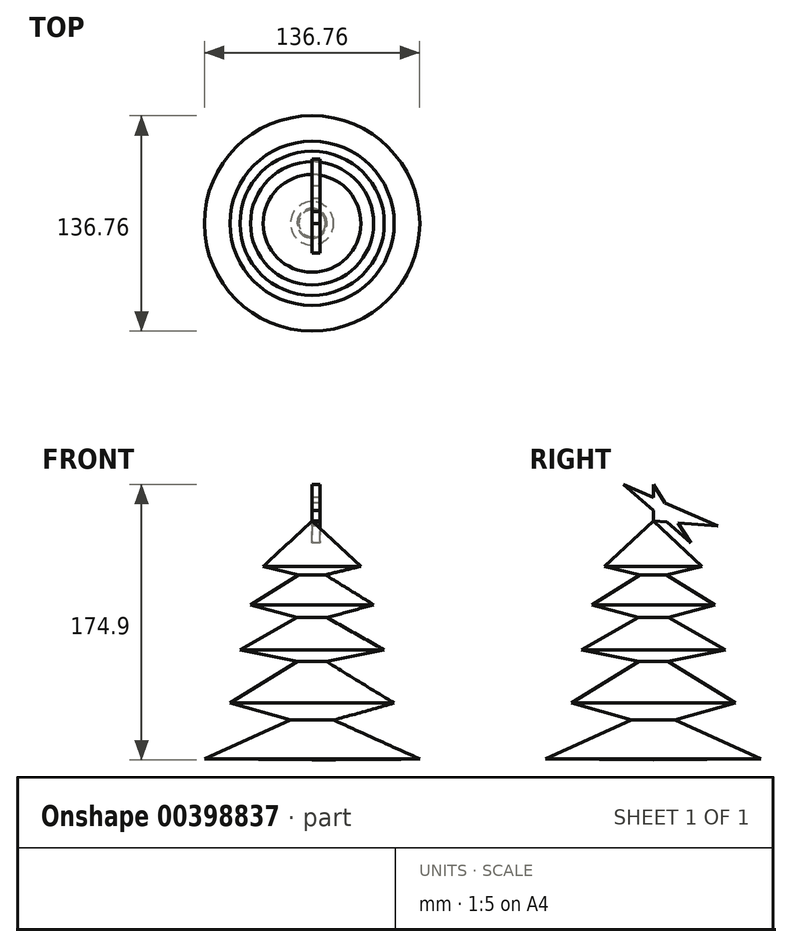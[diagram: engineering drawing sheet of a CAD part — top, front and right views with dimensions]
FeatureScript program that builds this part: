
annotation { "Feature Type Name" : "Feature", "Feature Type Description" : "" }
export const myFeature = defineFeature(function(context is Context, id is Id, definition is map)
    precondition{}
    {
        {
            var Q0;
            Q0=qCreatedBy(makeId("Front.planeOp"),FACE);
            var sketch = newSketch(context, id + "F0", { "sketchPlane" : qUnion([Q0])});
            skLineSegment(sketch, "E0", {"start": v(0, 75.99) * mm, "end": v(0, -75.59) * mm});
            skLineSegment(sketch, "E1", {"start": v(0, 75.99) * mm, "end": v(31.02, 47.38) * mm});
            skLineSegment(sketch, "E2", {"start": v(31.02, 47.38) * mm, "end": v(8.46, 41.92) * mm});
            skLineSegment(sketch, "E3", {"start": v(8.46, 41.92) * mm, "end": v(39.13, 22.93) * mm});
            skLineSegment(sketch, "E4", {"start": v(39.13, 22.93) * mm, "end": v(9.52, 14.73) * mm});
            skLineSegment(sketch, "E5", {"start": v(9.52, 14.73) * mm, "end": v(45.82, -5.8) * mm});
            skLineSegment(sketch, "E6", {"start": v(45.82, -5.8) * mm, "end": v(9.16, -13.22) * mm});
            skLineSegment(sketch, "E7", {"start": v(9.16, -13.22) * mm, "end": v(52.17, -39.58) * mm});
            skLineSegment(sketch, "E8", {"start": v(52.17, -39.58) * mm, "end": v(13.75, -50.32) * mm});
            skPoint(sketch, "E9.start.orphan", {"position": v(-4.58, -75.64) * mm});
            skPoint(sketch, "E10.end.orphan", {"position": v(49.35, -75.64) * mm});
            skLineSegment(sketch, "E11", {"start": v(13.75, -50.32) * mm, "end": v(68.38, -75.08) * mm});
            skLineSegment(sketch, "E12", {"start": v(68.38, -75.08) * mm, "end": v(0, -75.59) * mm});
            skSolve(sketch);
        }
        {
            var Q0;
            Q0=makeQuery(id+"F0.imprint","IMPRINT",FACE,{"disambiguationData":[TD([[makeQuery(id+"F0.imprint","IMPRINT",EDGE,{"derivedFrom":sQuery(id+"F0.wireOp",EDGE,"E0")}),1.0]])]});
            var Q1;
            Q1=sQuery(id+"F0.wireOp",EDGE,"E0");
            revolve(context, id + "F1", {"entities" : qUnion([Q0]), "axis" : qUnion([Q1]), "revolveType" : RevolveType.FULL});
        }
        {
            var Q0;
            Q0=qCreatedBy(makeId("Right.planeOp"),FACE);
            var sketch = newSketch(context, id + "F2", { "sketchPlane" : qUnion([Q0])});
            skLineSegment(sketch, "E13", {"start": v(0, 76.1) * mm, "end": v(0, 99.3) * mm});
            skLineSegment(sketch, "E14", {"start": v(0, 99.3) * mm, "end": v(23.81, 62.12) * mm});
            skLineSegment(sketch, "E15", {"start": v(23.81, 62.12) * mm, "end": v(-18.93, 99.3) * mm});
            skLineSegment(sketch, "E16", {"start": v(-18.93, 99.3) * mm, "end": v(40.9, 72.96) * mm});
            skLineSegment(sketch, "E17", {"start": v(40.9, 72.96) * mm, "end": v(0, 76.1) * mm});
            skSolve(sketch);
        }
        {
            var Q0;
            Q0 = qSketchRegion(id + "F2", true);
            extrude(context, id + "F3", {"entities" : qUnion([Q0]), "depth" : 5.08 * mm});
        }
    });
